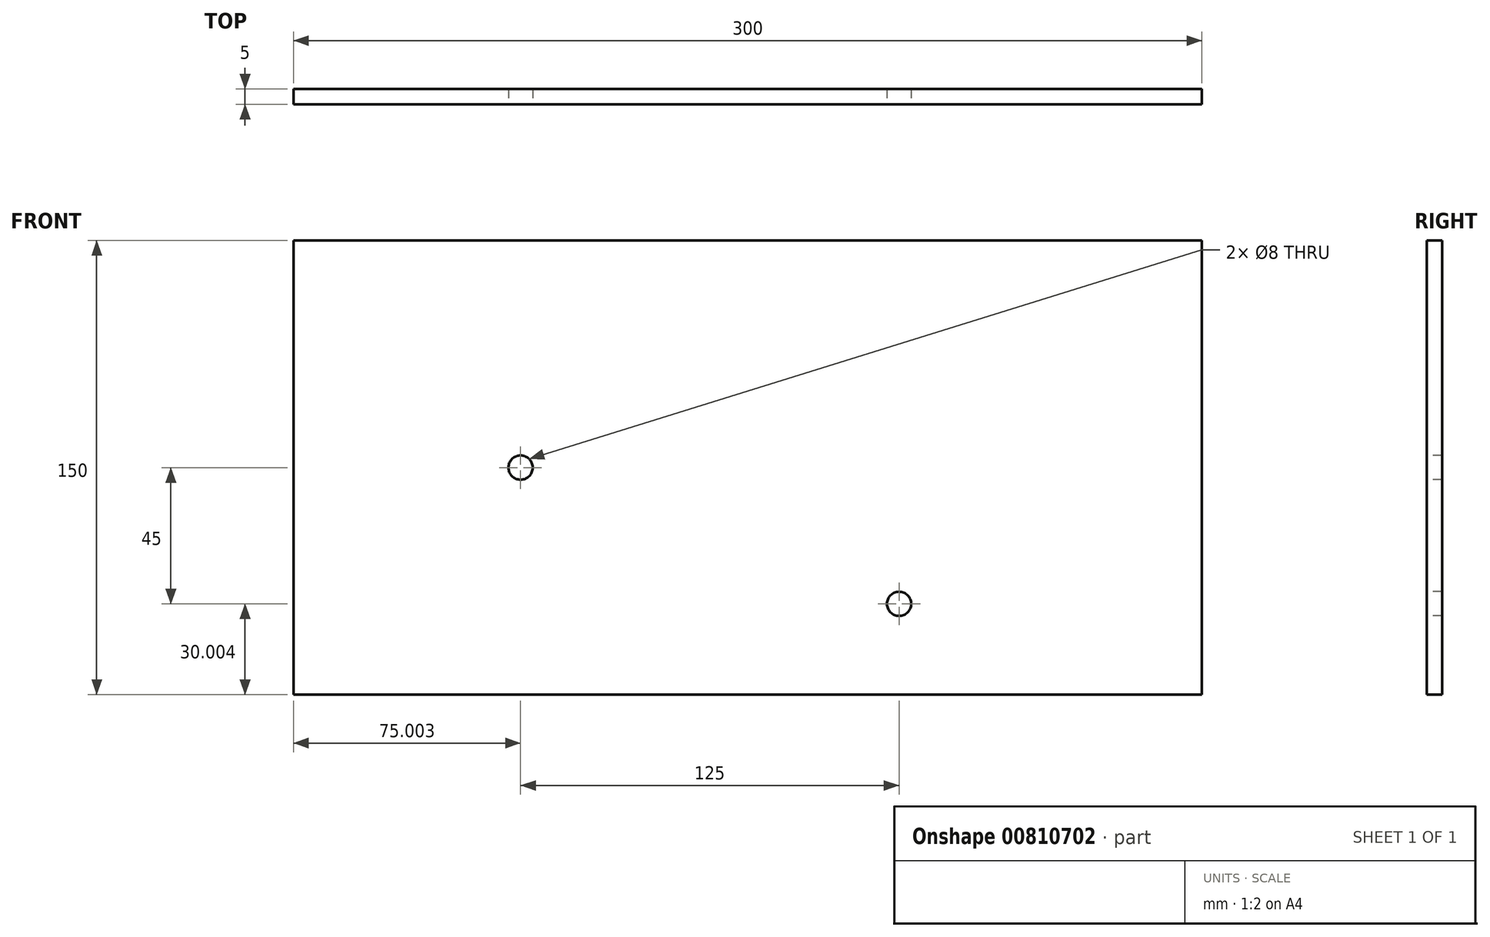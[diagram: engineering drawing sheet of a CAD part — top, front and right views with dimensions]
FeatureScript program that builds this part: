
annotation { "Feature Type Name" : "Feature", "Feature Type Description" : "" }
export const myFeature = defineFeature(function(context is Context, id is Id, definition is map)
    precondition{}
    {
        {
            var Q0;
            Q0=qCreatedBy(makeId("Front.planeOp"),FACE);
            var sketch = newSketch(context, id + "F0", { "sketchPlane" : qUnion([Q0])});
            skLineSegment(sketch, "E0.bottom", {"start": v(-165.87, 71.88) * mm, "end": v(134.13, 71.88) * mm});
            skLineSegment(sketch, "E0.top", {"start": v(-165.87, -78.12) * mm, "end": v(134.13, -78.12) * mm});
            skLineSegment(sketch, "E0.left", {"start": v(-165.87, 71.88) * mm, "end": v(-165.87, -78.12) * mm});
            skLineSegment(sketch, "E0.right", {"start": v(134.13, 71.88) * mm, "end": v(134.13, -78.12) * mm});
            skSolve(sketch);
        }
        {
            var Q0;
            Q0=makeQuery(id+"F0.imprint","IMPRINT",FACE,{"disambiguationData":[TD([[makeQuery(id+"F0.imprint","IMPRINT",EDGE,{"derivedFrom":sQuery(id+"F0.wireOp",EDGE,"E0.bottom")}),-1.0]])]});
            extrude(context, id + "F1", {"entities" : qUnion([Q0]), "depth" : 5 * mm, "offsetDistance" : 25 * mm});
        }
        {
            var Q0;
            Q0=makeQuery(id+"F1.opExtrude","CAP_FACE",FACE,{"disambiguationData":[OSD([sQuery(id+"F0.wireOp",EDGE,"E0.bottom"),sQuery(id+"F0.wireOp",EDGE,"E0.top"),sQuery(id+"F0.wireOp",EDGE,"E0.left"),sQuery(id+"F0.wireOp",EDGE,"E0.right")])],"isStart":false});
            var sketch = newSketch(context, id + "F2", { "sketchPlane" : qUnion([Q0])});
            skPoint(sketch, "E1", {"position": v(-90.87, -3.12) * mm});
            skPoint(sketch, "E2", {"position": v(34.13, -48.12) * mm});
            skSolve(sketch);
        }
        {
            var Q0;
            Q0=sQuery(id+"F2.wireOp",VERTEX,"E1");
            var Q1;
            Q1=sQuery(id+"F2.wireOp",VERTEX,"E2");
            var Q2;
            Q2=makeQuery(id+"F1.opExtrude","SWEPT_BODY",BODY,{"disambiguationData":[OSD([sQuery(id+"F0.wireOp",EDGE,"E0.bottom"),sQuery(id+"F0.wireOp",EDGE,"E0.top"),sQuery(id+"F0.wireOp",EDGE,"E0.left"),sQuery(id+"F0.wireOp",EDGE,"E0.right")])]});
            hole(context, id + "F3", {"style" : HoleStyle.SIMPLE, "endStyle" : HoleEndStyle.THROUGH, "holeDiameter" : 8 * mm, "majorDiameter" : 4 * mm, "isTappedThrough" : true, "tappedDepth" : 12 * mm, "tapClearance" : 3, "locations" : qUnion([Q0, Q1]), "scope" : qUnion([Q2])});
        }
    });
